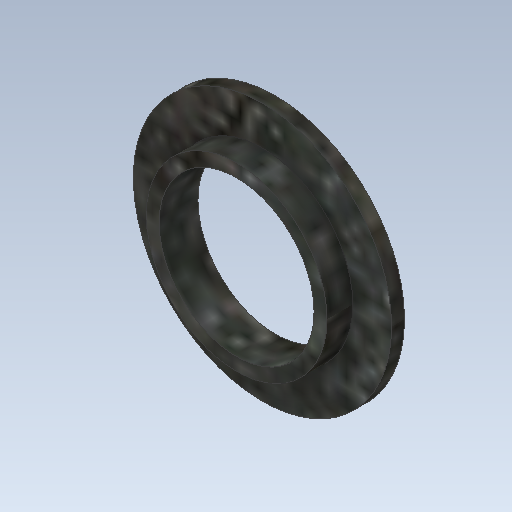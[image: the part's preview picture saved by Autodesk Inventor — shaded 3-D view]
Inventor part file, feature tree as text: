
AUTODESK INVENTOR PART (.ipt)
format: ipt  version: 2020.2 (Build 242310000, 310)  size: 174,080 bytes
history: native  units: mm
features: extrude x2, other x1, sketch x1
ambient origin geometry x8: Origin, YZ Plane, XZ Plane, XY Plane, X Axis, Y Axis, Z Axis, Center Point
bodies: Body1 (feature_tree)
feature tree (4):
  other  "ソリッド1"
  sketch  "スケッチ1"
  extrude  "押し出し1"  Depth=12.0mm
  extrude  "押し出し2"  Depth=14.0mm
